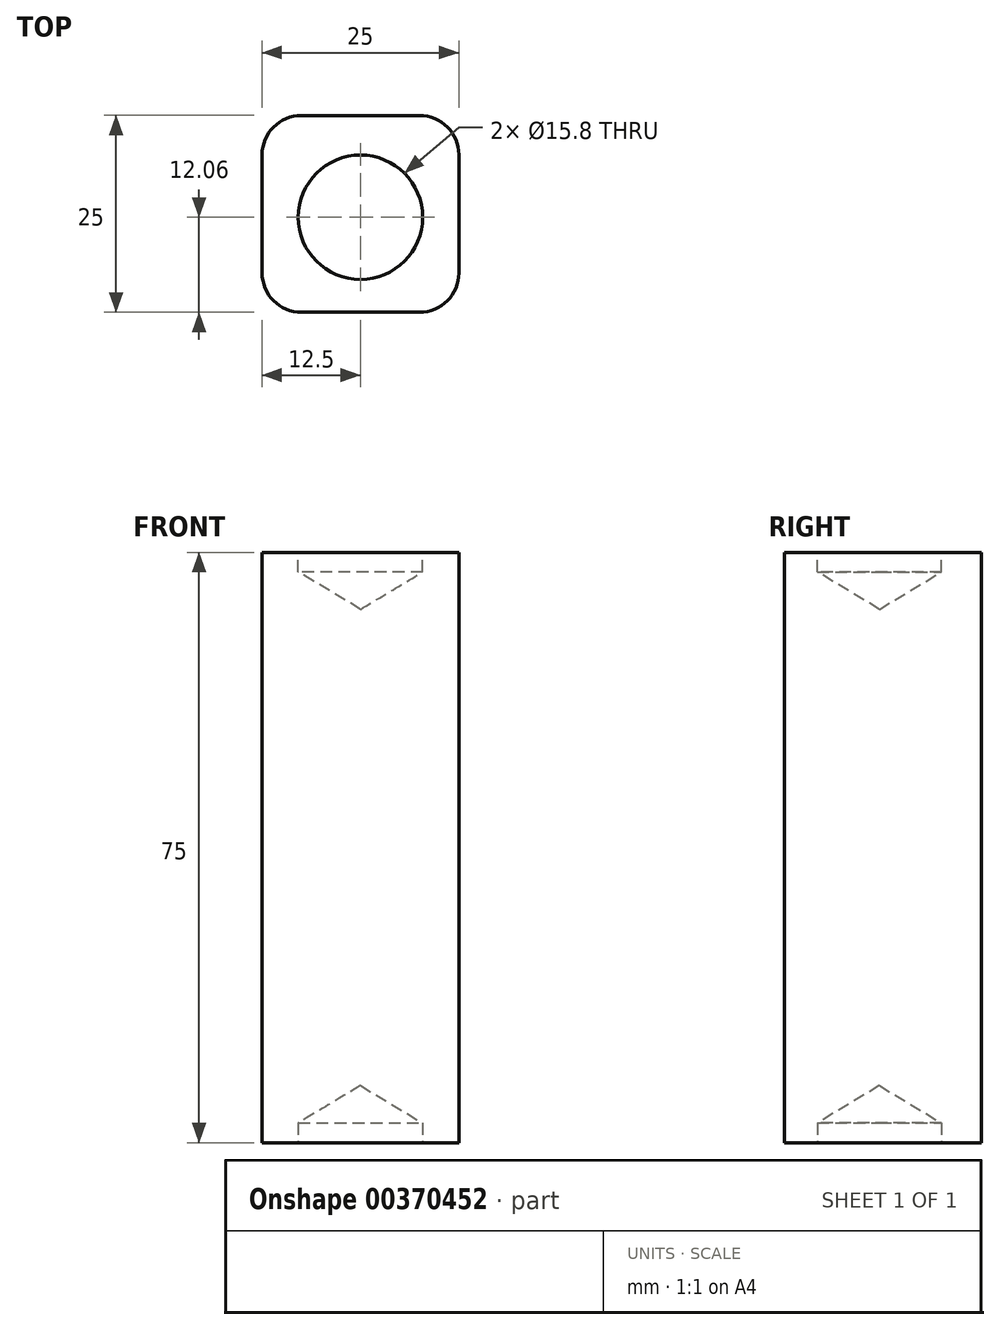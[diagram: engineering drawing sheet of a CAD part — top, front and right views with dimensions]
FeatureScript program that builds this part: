
annotation { "Feature Type Name" : "Feature", "Feature Type Description" : "" }
export const myFeature = defineFeature(function(context is Context, id is Id, definition is map)
    precondition{}
    {
        {
            var Q0;
            Q0=qCreatedBy(makeId("Top.planeOp"),FACE);
            var sketch = newSketch(context, id + "F0", { "sketchPlane" : qUnion([Q0])});
            skLineSegment(sketch, "E0.bottom", {"start": v(12.5, 12.94) * mm, "end": v(-12.5, 12.94) * mm});
            skLineSegment(sketch, "E0.top", {"start": v(12.5, -12.06) * mm, "end": v(-12.5, -12.06) * mm});
            skLineSegment(sketch, "E0.left", {"start": v(12.5, 12.94) * mm, "end": v(12.5, -12.06) * mm});
            skLineSegment(sketch, "E0.right", {"start": v(-12.5, 12.94) * mm, "end": v(-12.5, -12.06) * mm});
            skPoint(sketch, "E0.middle", {"position": v(0, 0.44) * mm});
            skSolve(sketch);
        }
        {
            var Q0;
            Q0=makeQuery(id+"F0.imprint","IMPRINT",FACE,{"disambiguationData":[TD([[makeQuery(id+"F0.imprint","IMPRINT",EDGE,{"derivedFrom":sQuery(id+"F0.wireOp",EDGE,"E0.bottom")}),1.0]])]});
            extrude(context, id + "F1", {"entities" : qUnion([Q0]), "depth" : 75 * mm});
        }
        {
            var Q0;
            Q0=makeQuery(id+"F1.opExtrude","CAP_FACE",FACE,{"disambiguationData":[OSD([sQuery(id+"F0.wireOp",EDGE,"E0.bottom"),sQuery(id+"F0.wireOp",EDGE,"E0.top"),sQuery(id+"F0.wireOp",EDGE,"E0.left"),sQuery(id+"F0.wireOp",EDGE,"E0.right")])],"isStart":true});
            var sketch = newSketch(context, id + "F2", { "sketchPlane" : qUnion([Q0])});
            skCircle(sketch, "E1", {"center": v(0, 0) * mm, "radius": 7.64 * mm});
            skSolve(sketch);
        }
        {
            var Q0;
            Q0=makeQuery(id+"F1.opExtrude","CAP_FACE",FACE,{"disambiguationData":[OSD([sQuery(id+"F0.wireOp",EDGE,"E0.bottom"),sQuery(id+"F0.wireOp",EDGE,"E0.top"),sQuery(id+"F0.wireOp",EDGE,"E0.left"),sQuery(id+"F0.wireOp",EDGE,"E0.right")])],"isStart":false});
            var sketch = newSketch(context, id + "F3", { "sketchPlane" : qUnion([Q0])});
            skCircle(sketch, "E2", {"center": v(0, 0) * mm, "radius": 4.1 * mm});
            skSolve(sketch);
        }
        {
            var Q0;
            Q0=sQuery(id+"F2.wireOp",VERTEX,"E1.center");
            var Q1;
            Q1=makeQuery(id+"F1.opExtrude","SWEPT_BODY",BODY,{"disambiguationData":[OSD([sQuery(id+"F0.wireOp",EDGE,"E0.bottom"),sQuery(id+"F0.wireOp",EDGE,"E0.top"),sQuery(id+"F0.wireOp",EDGE,"E0.left"),sQuery(id+"F0.wireOp",EDGE,"E0.right")])]});
            hole(context, id + "F4", {"style" : HoleStyle.SIMPLE, "endStyle" : HoleEndStyle.BLIND, "holeDiameter" : 15.8 * mm, "holeDepth" : 2.5 * mm, "tappedDepth" : 12 * mm, "tapClearance" : 3, "startFromSketch" : true, "locations" : qUnion([Q0]), "scope" : qUnion([Q1])});
        }
        {
            var Q0;
            Q0=sQuery(id+"F3.wireOp",VERTEX,"E2.center");
            var Q1;
            Q1=makeQuery(id+"F1.opExtrude","SWEPT_BODY",BODY,{"disambiguationData":[OSD([sQuery(id+"F0.wireOp",EDGE,"E0.bottom"),sQuery(id+"F0.wireOp",EDGE,"E0.top"),sQuery(id+"F0.wireOp",EDGE,"E0.left"),sQuery(id+"F0.wireOp",EDGE,"E0.right")])]});
            hole(context, id + "F5", {"style" : HoleStyle.SIMPLE, "endStyle" : HoleEndStyle.BLIND, "holeDiameter" : 15.8 * mm, "holeDepth" : 2.5 * mm, "tappedDepth" : 12 * mm, "tapClearance" : 3, "startFromSketch" : true, "locations" : qUnion([Q0]), "scope" : qUnion([Q1])});
        }
        {
            var Q0;
            Q0=makeQuery(id+"F1.opExtrude","SWEPT_EDGE",EDGE,{"disambiguationData":[OSD([sQuery(id+"F0.wireOp",EDGE,"E0.bottom"),sQuery(id+"F0.wireOp",EDGE,"E0.right")])]});
            var Q1;
            Q1=makeQuery(id+"F1.opExtrude","SWEPT_EDGE",EDGE,{"disambiguationData":[OSD([sQuery(id+"F0.wireOp",EDGE,"E0.top"),sQuery(id+"F0.wireOp",EDGE,"E0.right")])]});
            var Q2;
            Q2=makeQuery(id+"F1.opExtrude","SWEPT_EDGE",EDGE,{"disambiguationData":[OSD([sQuery(id+"F0.wireOp",EDGE,"E0.top"),sQuery(id+"F0.wireOp",EDGE,"E0.left")])]});
            var Q3;
            Q3=makeQuery(id+"F1.opExtrude","SWEPT_EDGE",EDGE,{"disambiguationData":[OSD([sQuery(id+"F0.wireOp",EDGE,"E0.bottom"),sQuery(id+"F0.wireOp",EDGE,"E0.left")])]});
            fillet(context, id + "F6", {"entities" : qUnion([Q0, Q1, Q2, Q3]), "radius" : 5 * mm, "tangentPropagation" : true, "allowEdgeOverflow" : false});
        }
    });
